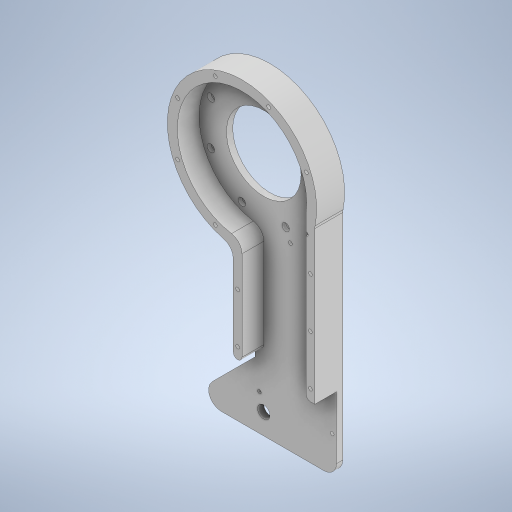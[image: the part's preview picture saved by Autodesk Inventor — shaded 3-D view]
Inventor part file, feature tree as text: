
AUTODESK INVENTOR PART (.ipt)
format: ipt  version: 2024.3 (Build 283343000, 343)  size: 479,744 bytes
history: native  units: mm
features: sketch x11, extrude x6, hole x5, fillet x3, other x1
ambient origin geometry x8: Origin, YZ Plane, XZ Plane, XY Plane, X Axis, Y Axis, Z Axis, Center Point
bodies: Body1 (feature_tree)
feature tree (26):
  other  "ソリッド1"
  extrude  "押し出し1"  Depth=120.0mm
  hole  "穴1"  [1 undecoded]
  extrude  "押し出し3"  Depth=5.0mm TaperAngle=0.0deg
  hole  "穴6"  [1 undecoded]
  hole  "穴7"  [1 undecoded]
  extrude  "押し出し10"  Depth=80.0mm TaperAngle=360.0deg
  extrude  "押し出し11"  Depth=58.5mm
  extrude  "押し出し12"  Depth=117.0mm
  hole  "穴8"  [1 undecoded]
  fillet  "フィレット4"  Radius=210.0mm
  fillet  "フィレット5"  Radius=5.0mm
  fillet  "フィレット6"  [1 undecoded]
  extrude  "押し出し13"  Depth=14.835299mm
  hole  "穴9"  [1 undecoded]
  sketch  "スケッチ1"
  sketch  "スケッチ2"
  sketch  "スケッチ4"
  sketch  "スケッチ15"
  sketch  "スケッチ16"
  sketch  "スケッチ17"
  sketch  "スケッチ18"
  sketch  "スケッチ19"
  sketch  "スケッチ20"
  sketch  "スケッチ21"
  sketch  "スケッチ22"
note: 6 required parameter values undecoded (feature->parameter linkage not recoverable at this tier; creation-order binding heuristic only, values carry confidence <= 0.55)
